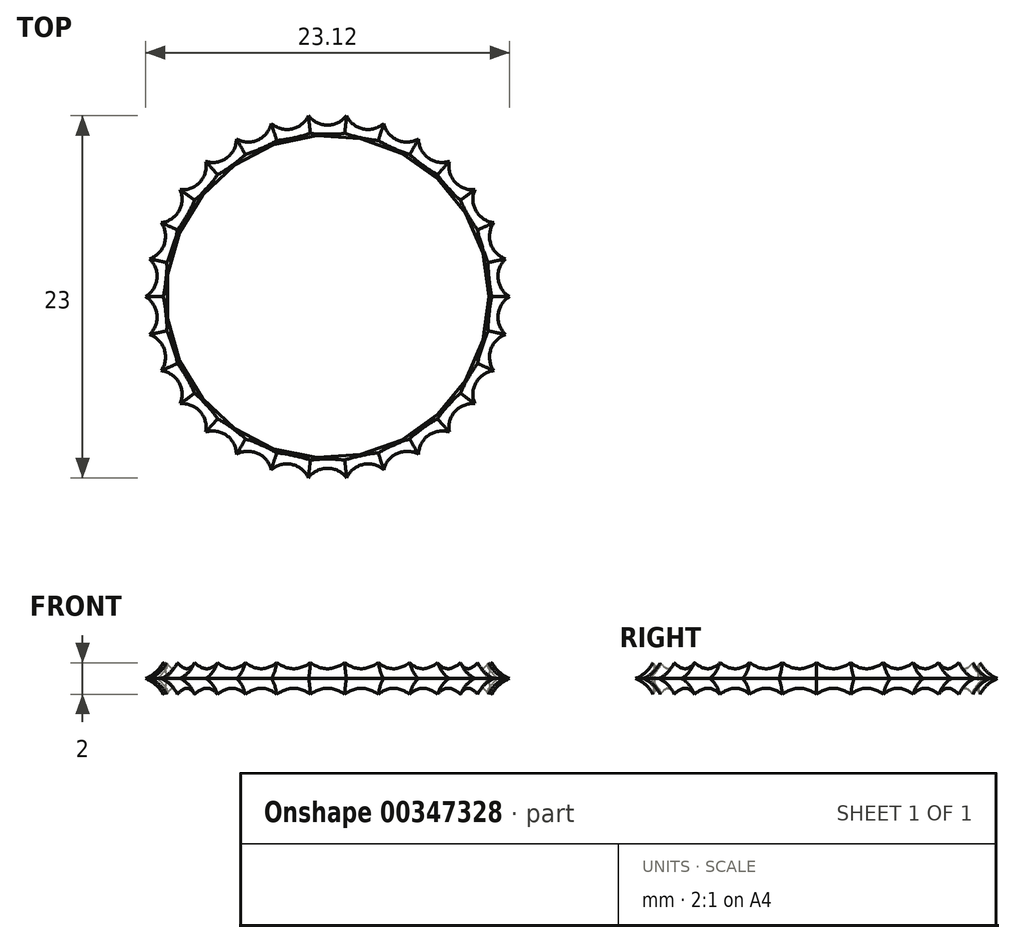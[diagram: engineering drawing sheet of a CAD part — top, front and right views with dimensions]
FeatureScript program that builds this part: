
annotation { "Feature Type Name" : "Feature", "Feature Type Description" : "" }
export const myFeature = defineFeature(function(context is Context, id is Id, definition is map)
    precondition{}
    {
        {
            var Q0;
            Q0=qCreatedBy(makeId("Front.planeOp"),FACE);
            var sketch = newSketch(context, id + "F0", { "sketchPlane" : qUnion([Q0])});
            skEllipse(sketch, "E0", {"center": v(11, 0) * mm, "majorRadius": 1.5 * mm, "minorRadius": 0.75 * mm, "majorAxis": v(0, 1)});
            skLineSegment(sketch, "E1", {"start": v(0, 20.87) * mm, "end": v(0, -23.5) * mm, "construction": true});
            skSolve(sketch);
        }
        {
            var Q0;
            Q0=makeQuery(id+"F0.imprint","IMPRINT",FACE,{"disambiguationData":[TD([[makeQuery(id+"F0.imprint","IMPRINT",EDGE,{"derivedFrom":sQuery(id+"F0.wireOp",EDGE,"E0")}),1.0]])]});
            var Q1;
            Q1=sQuery(id+"F0.wireOp",EDGE,"E1");
            revolve(context, id + "F1", {"entities" : qUnion([Q0]), "axis" : qUnion([Q1]), "revolveType" : RevolveType.FULL});
        }
        {
            var Q0;
            Q0=qCreatedBy(makeId("Right.planeOp"),FACE);
            var sketch = newSketch(context, id + "F2", { "sketchPlane" : qUnion([Q0])});
            skLineSegment(sketch, "E2", {"start": v(-11.23, 6.03) * mm, "end": v(-12.18, -4.75) * mm, "construction": true});
            skEllipse(sketch, "E3", {"center": v(-11, 0) * mm, "majorRadius": 1.5 * mm, "minorRadius": 0.75 * mm, "majorAxis": v(0, 1)});
            skLineSegment(sketch, "E4", {"start": v(-17.41, -3.3) * mm, "end": v(-16.66, 5.3) * mm});
            skSolve(sketch);
        }
        {
            var Q0;
            Q0=sQuery(id+"F2.wireOp",EDGE,"E4");
            cPlane(context, id + "F3", {"entities" : qUnion([Q0]), "cplaneType" : CPlaneType.LINE_ANGLE, "offset" : 25 * mm, "angle" : 90 * degree, "width" : 150 * mm, "height" : 150 * mm});
        }
        {
            var Q0;
            Q0=qCreatedBy(id+"F3.planeOp",FACE);
            var sketch = newSketch(context, id + "F4", { "sketchPlane" : qUnion([Q0])});
            skEllipticalArc(sketch, "E5", {});
            skPoint(sketch, "E6.firstSnap0", {"position": v(0, -8.8) * mm});
            skLineSegment(sketch, "E7", {"start": v(0, -3.31) * mm, "end": v(0, -10.23) * mm, "construction": true});
            skLineSegment(sketch, "E8", {"start": v(0, -3.8) * mm, "end": v(0, -8.8) * mm});
            const initialGuessF4  = {"E5": [0, -0.006309002116322518, 0, 1, 0.0025, 0.0025, 0, 3.141592653589793]};
            skSetInitialGuess(sketch, initialGuessF4);
            skSolve(sketch);
        }
        {
            var Q0;
            Q0 = qSketchRegion(id + "F4", true);
            var Q1;
            Q1=sQuery(id+"F2.wireOp",EDGE,"E4");
            revolve(context, id + "F5", {"entities" : qUnion([Q0]), "axis" : qUnion([Q1]), "revolveType" : RevolveType.FULL});
        }
        {
            var Q0;
            Q0=makeQuery(id+"F5.opRevolve","SWEPT_BODY",BODY,{"disambiguationData":[OSD([sQuery(id+"F4.wireOp",EDGE,"E5"),sQuery(id+"F4.wireOp",EDGE,"E8")])]});
            transform(context, id + "F6", {"entities" : qUnion([Q0]), "transformType" : TransformType.TRANSLATION_3D, "dx" : 0 * mm, "dy" : 5.14 * mm, "dz" : 6.8 * mm, "makeCopy" : false});
        }
        {
            var Q0;
            Q0=makeQuery(id+"F5.opRevolve","SWEPT_BODY",BODY,{"disambiguationData":[OSD([sQuery(id+"F4.wireOp",EDGE,"E5"),sQuery(id+"F4.wireOp",EDGE,"E8")])]});
            var Q1;
            Q1=sQuery(id+"F0.wireOp",EDGE,"E1");
            circularPattern(context, id + "F7", {"entities" : qUnion([Q0]), "axis" : qUnion([Q1]), "angle" : 360 * degree, "instanceCount" : 30, "equalSpace" : true});
        }
        {
            var Q0;
            Q0=makeQuery(id+"F5.opRevolve","SWEPT_BODY",BODY,{"disambiguationData":[OSD([sQuery(id+"F4.wireOp",EDGE,"E5"),sQuery(id+"F4.wireOp",EDGE,"E8")])]});
            var Q1;
            Q1=makeQuery(id+"F7.opPattern","COPY",BODY,{"derivedFrom":makeQuery(id+"F5.opRevolve","SWEPT_BODY",BODY,{"disambiguationData":[OSD([sQuery(id+"F4.wireOp",EDGE,"E5"),sQuery(id+"F4.wireOp",EDGE,"E8")])]}),"instanceName":"1"});
            var Q2;
            Q2=makeQuery(id+"F7.opPattern","COPY",BODY,{"derivedFrom":makeQuery(id+"F5.opRevolve","SWEPT_BODY",BODY,{"disambiguationData":[OSD([sQuery(id+"F4.wireOp",EDGE,"E5"),sQuery(id+"F4.wireOp",EDGE,"E8")])]}),"instanceName":"2"});
            var Q3;
            Q3=makeQuery(id+"F7.opPattern","COPY",BODY,{"derivedFrom":makeQuery(id+"F5.opRevolve","SWEPT_BODY",BODY,{"disambiguationData":[OSD([sQuery(id+"F4.wireOp",EDGE,"E5"),sQuery(id+"F4.wireOp",EDGE,"E8")])]}),"instanceName":"3"});
            var Q4;
            Q4=makeQuery(id+"F7.opPattern","COPY",BODY,{"derivedFrom":makeQuery(id+"F5.opRevolve","SWEPT_BODY",BODY,{"disambiguationData":[OSD([sQuery(id+"F4.wireOp",EDGE,"E5"),sQuery(id+"F4.wireOp",EDGE,"E8")])]}),"instanceName":"4"});
            var Q5;
            Q5=makeQuery(id+"F7.opPattern","COPY",BODY,{"derivedFrom":makeQuery(id+"F5.opRevolve","SWEPT_BODY",BODY,{"disambiguationData":[OSD([sQuery(id+"F4.wireOp",EDGE,"E5"),sQuery(id+"F4.wireOp",EDGE,"E8")])]}),"instanceName":"5"});
            var Q6;
            Q6=makeQuery(id+"F7.opPattern","COPY",BODY,{"derivedFrom":makeQuery(id+"F5.opRevolve","SWEPT_BODY",BODY,{"disambiguationData":[OSD([sQuery(id+"F4.wireOp",EDGE,"E5"),sQuery(id+"F4.wireOp",EDGE,"E8")])]}),"instanceName":"6"});
            var Q7;
            Q7=makeQuery(id+"F7.opPattern","COPY",BODY,{"derivedFrom":makeQuery(id+"F5.opRevolve","SWEPT_BODY",BODY,{"disambiguationData":[OSD([sQuery(id+"F4.wireOp",EDGE,"E5"),sQuery(id+"F4.wireOp",EDGE,"E8")])]}),"instanceName":"7"});
            var Q8;
            Q8=makeQuery(id+"F7.opPattern","COPY",BODY,{"derivedFrom":makeQuery(id+"F5.opRevolve","SWEPT_BODY",BODY,{"disambiguationData":[OSD([sQuery(id+"F4.wireOp",EDGE,"E5"),sQuery(id+"F4.wireOp",EDGE,"E8")])]}),"instanceName":"8"});
            var Q9;
            Q9=makeQuery(id+"F7.opPattern","COPY",BODY,{"derivedFrom":makeQuery(id+"F5.opRevolve","SWEPT_BODY",BODY,{"disambiguationData":[OSD([sQuery(id+"F4.wireOp",EDGE,"E5"),sQuery(id+"F4.wireOp",EDGE,"E8")])]}),"instanceName":"9"});
            var Q10;
            Q10=makeQuery(id+"F7.opPattern","COPY",BODY,{"derivedFrom":makeQuery(id+"F5.opRevolve","SWEPT_BODY",BODY,{"disambiguationData":[OSD([sQuery(id+"F4.wireOp",EDGE,"E5"),sQuery(id+"F4.wireOp",EDGE,"E8")])]}),"instanceName":"10"});
            var Q11;
            Q11=makeQuery(id+"F7.opPattern","COPY",BODY,{"derivedFrom":makeQuery(id+"F5.opRevolve","SWEPT_BODY",BODY,{"disambiguationData":[OSD([sQuery(id+"F4.wireOp",EDGE,"E5"),sQuery(id+"F4.wireOp",EDGE,"E8")])]}),"instanceName":"11"});
            var Q12;
            Q12=makeQuery(id+"F7.opPattern","COPY",BODY,{"derivedFrom":makeQuery(id+"F5.opRevolve","SWEPT_BODY",BODY,{"disambiguationData":[OSD([sQuery(id+"F4.wireOp",EDGE,"E5"),sQuery(id+"F4.wireOp",EDGE,"E8")])]}),"instanceName":"12"});
            var Q13;
            Q13=makeQuery(id+"F7.opPattern","COPY",BODY,{"derivedFrom":makeQuery(id+"F5.opRevolve","SWEPT_BODY",BODY,{"disambiguationData":[OSD([sQuery(id+"F4.wireOp",EDGE,"E5"),sQuery(id+"F4.wireOp",EDGE,"E8")])]}),"instanceName":"13"});
            var Q14;
            Q14=makeQuery(id+"F7.opPattern","COPY",BODY,{"derivedFrom":makeQuery(id+"F5.opRevolve","SWEPT_BODY",BODY,{"disambiguationData":[OSD([sQuery(id+"F4.wireOp",EDGE,"E5"),sQuery(id+"F4.wireOp",EDGE,"E8")])]}),"instanceName":"14"});
            var Q15;
            Q15=makeQuery(id+"F7.opPattern","COPY",BODY,{"derivedFrom":makeQuery(id+"F5.opRevolve","SWEPT_BODY",BODY,{"disambiguationData":[OSD([sQuery(id+"F4.wireOp",EDGE,"E5"),sQuery(id+"F4.wireOp",EDGE,"E8")])]}),"instanceName":"15"});
            var Q16;
            Q16=makeQuery(id+"F7.opPattern","COPY",BODY,{"derivedFrom":makeQuery(id+"F5.opRevolve","SWEPT_BODY",BODY,{"disambiguationData":[OSD([sQuery(id+"F4.wireOp",EDGE,"E5"),sQuery(id+"F4.wireOp",EDGE,"E8")])]}),"instanceName":"16"});
            var Q17;
            Q17=makeQuery(id+"F7.opPattern","COPY",BODY,{"derivedFrom":makeQuery(id+"F5.opRevolve","SWEPT_BODY",BODY,{"disambiguationData":[OSD([sQuery(id+"F4.wireOp",EDGE,"E5"),sQuery(id+"F4.wireOp",EDGE,"E8")])]}),"instanceName":"17"});
            var Q18;
            Q18=makeQuery(id+"F7.opPattern","COPY",BODY,{"derivedFrom":makeQuery(id+"F5.opRevolve","SWEPT_BODY",BODY,{"disambiguationData":[OSD([sQuery(id+"F4.wireOp",EDGE,"E5"),sQuery(id+"F4.wireOp",EDGE,"E8")])]}),"instanceName":"18"});
            var Q19;
            Q19=makeQuery(id+"F7.opPattern","COPY",BODY,{"derivedFrom":makeQuery(id+"F5.opRevolve","SWEPT_BODY",BODY,{"disambiguationData":[OSD([sQuery(id+"F4.wireOp",EDGE,"E5"),sQuery(id+"F4.wireOp",EDGE,"E8")])]}),"instanceName":"19"});
            var Q20;
            Q20=makeQuery(id+"F7.opPattern","COPY",BODY,{"derivedFrom":makeQuery(id+"F5.opRevolve","SWEPT_BODY",BODY,{"disambiguationData":[OSD([sQuery(id+"F4.wireOp",EDGE,"E5"),sQuery(id+"F4.wireOp",EDGE,"E8")])]}),"instanceName":"20"});
            var Q21;
            Q21=makeQuery(id+"F7.opPattern","COPY",BODY,{"derivedFrom":makeQuery(id+"F5.opRevolve","SWEPT_BODY",BODY,{"disambiguationData":[OSD([sQuery(id+"F4.wireOp",EDGE,"E5"),sQuery(id+"F4.wireOp",EDGE,"E8")])]}),"instanceName":"21"});
            var Q22;
            Q22=makeQuery(id+"F7.opPattern","COPY",BODY,{"derivedFrom":makeQuery(id+"F5.opRevolve","SWEPT_BODY",BODY,{"disambiguationData":[OSD([sQuery(id+"F4.wireOp",EDGE,"E5"),sQuery(id+"F4.wireOp",EDGE,"E8")])]}),"instanceName":"22"});
            var Q23;
            Q23=makeQuery(id+"F7.opPattern","COPY",BODY,{"derivedFrom":makeQuery(id+"F5.opRevolve","SWEPT_BODY",BODY,{"disambiguationData":[OSD([sQuery(id+"F4.wireOp",EDGE,"E5"),sQuery(id+"F4.wireOp",EDGE,"E8")])]}),"instanceName":"23"});
            var Q24;
            Q24=makeQuery(id+"F7.opPattern","COPY",BODY,{"derivedFrom":makeQuery(id+"F5.opRevolve","SWEPT_BODY",BODY,{"disambiguationData":[OSD([sQuery(id+"F4.wireOp",EDGE,"E5"),sQuery(id+"F4.wireOp",EDGE,"E8")])]}),"instanceName":"24"});
            var Q25;
            Q25=makeQuery(id+"F7.opPattern","COPY",BODY,{"derivedFrom":makeQuery(id+"F5.opRevolve","SWEPT_BODY",BODY,{"disambiguationData":[OSD([sQuery(id+"F4.wireOp",EDGE,"E5"),sQuery(id+"F4.wireOp",EDGE,"E8")])]}),"instanceName":"25"});
            var Q26;
            Q26=makeQuery(id+"F7.opPattern","COPY",BODY,{"derivedFrom":makeQuery(id+"F5.opRevolve","SWEPT_BODY",BODY,{"disambiguationData":[OSD([sQuery(id+"F4.wireOp",EDGE,"E5"),sQuery(id+"F4.wireOp",EDGE,"E8")])]}),"instanceName":"26"});
            var Q27;
            Q27=makeQuery(id+"F7.opPattern","COPY",BODY,{"derivedFrom":makeQuery(id+"F5.opRevolve","SWEPT_BODY",BODY,{"disambiguationData":[OSD([sQuery(id+"F4.wireOp",EDGE,"E5"),sQuery(id+"F4.wireOp",EDGE,"E8")])]}),"instanceName":"27"});
            var Q28;
            Q28=makeQuery(id+"F7.opPattern","COPY",BODY,{"derivedFrom":makeQuery(id+"F5.opRevolve","SWEPT_BODY",BODY,{"disambiguationData":[OSD([sQuery(id+"F4.wireOp",EDGE,"E5"),sQuery(id+"F4.wireOp",EDGE,"E8")])]}),"instanceName":"28"});
            var Q29;
            Q29=makeQuery(id+"F7.opPattern","COPY",BODY,{"derivedFrom":makeQuery(id+"F5.opRevolve","SWEPT_BODY",BODY,{"disambiguationData":[OSD([sQuery(id+"F4.wireOp",EDGE,"E5"),sQuery(id+"F4.wireOp",EDGE,"E8")])]}),"instanceName":"29"});
            var Q30;
            Q30=qCreatedBy(makeId("Top.planeOp"),FACE);
            mirror(context, id + "F8", {"entities" : qUnion([Q0, Q1, Q2, Q3, Q4, Q5, Q6, Q7, Q8, Q9, Q10, Q11, Q12, Q13, Q14, Q15, Q16, Q17, Q18, Q19, Q20, Q21, Q22, Q23, Q24, Q25, Q26, Q27, Q28, Q29]), "mirrorPlane" : qUnion([Q30])});
        }
        {
            var Q0;
            Q0=makeQuery(id+"F5.opRevolve","SWEPT_BODY",BODY,{"disambiguationData":[OSD([sQuery(id+"F4.wireOp",EDGE,"E5"),sQuery(id+"F4.wireOp",EDGE,"E8")])]});
            var Q1;
            Q1=makeQuery(id+"F7.opPattern","COPY",BODY,{"derivedFrom":makeQuery(id+"F5.opRevolve","SWEPT_BODY",BODY,{"disambiguationData":[OSD([sQuery(id+"F4.wireOp",EDGE,"E5"),sQuery(id+"F4.wireOp",EDGE,"E8")])]}),"instanceName":"1"});
            var Q2;
            Q2=makeQuery(id+"F7.opPattern","COPY",BODY,{"derivedFrom":makeQuery(id+"F5.opRevolve","SWEPT_BODY",BODY,{"disambiguationData":[OSD([sQuery(id+"F4.wireOp",EDGE,"E5"),sQuery(id+"F4.wireOp",EDGE,"E8")])]}),"instanceName":"2"});
            var Q3;
            Q3=makeQuery(id+"F7.opPattern","COPY",BODY,{"derivedFrom":makeQuery(id+"F5.opRevolve","SWEPT_BODY",BODY,{"disambiguationData":[OSD([sQuery(id+"F4.wireOp",EDGE,"E5"),sQuery(id+"F4.wireOp",EDGE,"E8")])]}),"instanceName":"3"});
            var Q4;
            Q4=makeQuery(id+"F7.opPattern","COPY",BODY,{"derivedFrom":makeQuery(id+"F5.opRevolve","SWEPT_BODY",BODY,{"disambiguationData":[OSD([sQuery(id+"F4.wireOp",EDGE,"E5"),sQuery(id+"F4.wireOp",EDGE,"E8")])]}),"instanceName":"4"});
            var Q5;
            Q5=makeQuery(id+"F7.opPattern","COPY",BODY,{"derivedFrom":makeQuery(id+"F5.opRevolve","SWEPT_BODY",BODY,{"disambiguationData":[OSD([sQuery(id+"F4.wireOp",EDGE,"E5"),sQuery(id+"F4.wireOp",EDGE,"E8")])]}),"instanceName":"5"});
            var Q6;
            Q6=makeQuery(id+"F7.opPattern","COPY",BODY,{"derivedFrom":makeQuery(id+"F5.opRevolve","SWEPT_BODY",BODY,{"disambiguationData":[OSD([sQuery(id+"F4.wireOp",EDGE,"E5"),sQuery(id+"F4.wireOp",EDGE,"E8")])]}),"instanceName":"6"});
            var Q7;
            Q7=makeQuery(id+"F7.opPattern","COPY",BODY,{"derivedFrom":makeQuery(id+"F5.opRevolve","SWEPT_BODY",BODY,{"disambiguationData":[OSD([sQuery(id+"F4.wireOp",EDGE,"E5"),sQuery(id+"F4.wireOp",EDGE,"E8")])]}),"instanceName":"7"});
            var Q8;
            Q8=makeQuery(id+"F7.opPattern","COPY",BODY,{"derivedFrom":makeQuery(id+"F5.opRevolve","SWEPT_BODY",BODY,{"disambiguationData":[OSD([sQuery(id+"F4.wireOp",EDGE,"E5"),sQuery(id+"F4.wireOp",EDGE,"E8")])]}),"instanceName":"8"});
            var Q9;
            Q9=makeQuery(id+"F7.opPattern","COPY",BODY,{"derivedFrom":makeQuery(id+"F5.opRevolve","SWEPT_BODY",BODY,{"disambiguationData":[OSD([sQuery(id+"F4.wireOp",EDGE,"E5"),sQuery(id+"F4.wireOp",EDGE,"E8")])]}),"instanceName":"9"});
            var Q10;
            Q10=makeQuery(id+"F7.opPattern","COPY",BODY,{"derivedFrom":makeQuery(id+"F5.opRevolve","SWEPT_BODY",BODY,{"disambiguationData":[OSD([sQuery(id+"F4.wireOp",EDGE,"E5"),sQuery(id+"F4.wireOp",EDGE,"E8")])]}),"instanceName":"10"});
            var Q11;
            Q11=makeQuery(id+"F7.opPattern","COPY",BODY,{"derivedFrom":makeQuery(id+"F5.opRevolve","SWEPT_BODY",BODY,{"disambiguationData":[OSD([sQuery(id+"F4.wireOp",EDGE,"E5"),sQuery(id+"F4.wireOp",EDGE,"E8")])]}),"instanceName":"11"});
            var Q12;
            Q12=makeQuery(id+"F7.opPattern","COPY",BODY,{"derivedFrom":makeQuery(id+"F5.opRevolve","SWEPT_BODY",BODY,{"disambiguationData":[OSD([sQuery(id+"F4.wireOp",EDGE,"E5"),sQuery(id+"F4.wireOp",EDGE,"E8")])]}),"instanceName":"12"});
            var Q13;
            Q13=makeQuery(id+"F7.opPattern","COPY",BODY,{"derivedFrom":makeQuery(id+"F5.opRevolve","SWEPT_BODY",BODY,{"disambiguationData":[OSD([sQuery(id+"F4.wireOp",EDGE,"E5"),sQuery(id+"F4.wireOp",EDGE,"E8")])]}),"instanceName":"13"});
            var Q14;
            Q14=makeQuery(id+"F7.opPattern","COPY",BODY,{"derivedFrom":makeQuery(id+"F5.opRevolve","SWEPT_BODY",BODY,{"disambiguationData":[OSD([sQuery(id+"F4.wireOp",EDGE,"E5"),sQuery(id+"F4.wireOp",EDGE,"E8")])]}),"instanceName":"14"});
            var Q15;
            Q15=makeQuery(id+"F7.opPattern","COPY",BODY,{"derivedFrom":makeQuery(id+"F5.opRevolve","SWEPT_BODY",BODY,{"disambiguationData":[OSD([sQuery(id+"F4.wireOp",EDGE,"E5"),sQuery(id+"F4.wireOp",EDGE,"E8")])]}),"instanceName":"15"});
            var Q16;
            Q16=makeQuery(id+"F7.opPattern","COPY",BODY,{"derivedFrom":makeQuery(id+"F5.opRevolve","SWEPT_BODY",BODY,{"disambiguationData":[OSD([sQuery(id+"F4.wireOp",EDGE,"E5"),sQuery(id+"F4.wireOp",EDGE,"E8")])]}),"instanceName":"16"});
            var Q17;
            Q17=makeQuery(id+"F7.opPattern","COPY",BODY,{"derivedFrom":makeQuery(id+"F5.opRevolve","SWEPT_BODY",BODY,{"disambiguationData":[OSD([sQuery(id+"F4.wireOp",EDGE,"E5"),sQuery(id+"F4.wireOp",EDGE,"E8")])]}),"instanceName":"17"});
            var Q18;
            Q18=makeQuery(id+"F7.opPattern","COPY",BODY,{"derivedFrom":makeQuery(id+"F5.opRevolve","SWEPT_BODY",BODY,{"disambiguationData":[OSD([sQuery(id+"F4.wireOp",EDGE,"E5"),sQuery(id+"F4.wireOp",EDGE,"E8")])]}),"instanceName":"18"});
            var Q19;
            Q19=makeQuery(id+"F7.opPattern","COPY",BODY,{"derivedFrom":makeQuery(id+"F5.opRevolve","SWEPT_BODY",BODY,{"disambiguationData":[OSD([sQuery(id+"F4.wireOp",EDGE,"E5"),sQuery(id+"F4.wireOp",EDGE,"E8")])]}),"instanceName":"19"});
            var Q20;
            Q20=makeQuery(id+"F7.opPattern","COPY",BODY,{"derivedFrom":makeQuery(id+"F5.opRevolve","SWEPT_BODY",BODY,{"disambiguationData":[OSD([sQuery(id+"F4.wireOp",EDGE,"E5"),sQuery(id+"F4.wireOp",EDGE,"E8")])]}),"instanceName":"20"});
            var Q21;
            Q21=makeQuery(id+"F7.opPattern","COPY",BODY,{"derivedFrom":makeQuery(id+"F5.opRevolve","SWEPT_BODY",BODY,{"disambiguationData":[OSD([sQuery(id+"F4.wireOp",EDGE,"E5"),sQuery(id+"F4.wireOp",EDGE,"E8")])]}),"instanceName":"21"});
            var Q22;
            Q22=makeQuery(id+"F7.opPattern","COPY",BODY,{"derivedFrom":makeQuery(id+"F5.opRevolve","SWEPT_BODY",BODY,{"disambiguationData":[OSD([sQuery(id+"F4.wireOp",EDGE,"E5"),sQuery(id+"F4.wireOp",EDGE,"E8")])]}),"instanceName":"22"});
            var Q23;
            Q23=makeQuery(id+"F7.opPattern","COPY",BODY,{"derivedFrom":makeQuery(id+"F5.opRevolve","SWEPT_BODY",BODY,{"disambiguationData":[OSD([sQuery(id+"F4.wireOp",EDGE,"E5"),sQuery(id+"F4.wireOp",EDGE,"E8")])]}),"instanceName":"23"});
            var Q24;
            Q24=makeQuery(id+"F7.opPattern","COPY",BODY,{"derivedFrom":makeQuery(id+"F5.opRevolve","SWEPT_BODY",BODY,{"disambiguationData":[OSD([sQuery(id+"F4.wireOp",EDGE,"E5"),sQuery(id+"F4.wireOp",EDGE,"E8")])]}),"instanceName":"24"});
            var Q25;
            Q25=makeQuery(id+"F7.opPattern","COPY",BODY,{"derivedFrom":makeQuery(id+"F5.opRevolve","SWEPT_BODY",BODY,{"disambiguationData":[OSD([sQuery(id+"F4.wireOp",EDGE,"E5"),sQuery(id+"F4.wireOp",EDGE,"E8")])]}),"instanceName":"25"});
            var Q26;
            Q26=makeQuery(id+"F7.opPattern","COPY",BODY,{"derivedFrom":makeQuery(id+"F5.opRevolve","SWEPT_BODY",BODY,{"disambiguationData":[OSD([sQuery(id+"F4.wireOp",EDGE,"E5"),sQuery(id+"F4.wireOp",EDGE,"E8")])]}),"instanceName":"26"});
            var Q27;
            Q27=makeQuery(id+"F7.opPattern","COPY",BODY,{"derivedFrom":makeQuery(id+"F5.opRevolve","SWEPT_BODY",BODY,{"disambiguationData":[OSD([sQuery(id+"F4.wireOp",EDGE,"E5"),sQuery(id+"F4.wireOp",EDGE,"E8")])]}),"instanceName":"27"});
            var Q28;
            Q28=makeQuery(id+"F7.opPattern","COPY",BODY,{"derivedFrom":makeQuery(id+"F5.opRevolve","SWEPT_BODY",BODY,{"disambiguationData":[OSD([sQuery(id+"F4.wireOp",EDGE,"E5"),sQuery(id+"F4.wireOp",EDGE,"E8")])]}),"instanceName":"28"});
            var Q29;
            Q29=makeQuery(id+"F7.opPattern","COPY",BODY,{"derivedFrom":makeQuery(id+"F5.opRevolve","SWEPT_BODY",BODY,{"disambiguationData":[OSD([sQuery(id+"F4.wireOp",EDGE,"E5"),sQuery(id+"F4.wireOp",EDGE,"E8")])]}),"instanceName":"29"});
            var Q30;
            Q30=makeQuery(id+"F8.opPattern","COPY",BODY,{"derivedFrom":makeQuery(id+"F5.opRevolve","SWEPT_BODY",BODY,{"disambiguationData":[OSD([sQuery(id+"F4.wireOp",EDGE,"E5"),sQuery(id+"F4.wireOp",EDGE,"E8")])]}),"instanceName":"1"});
            var Q31;
            Q31=makeQuery(id+"F8.opPattern","COPY",BODY,{"derivedFrom":makeQuery(id+"F7.opPattern","COPY",BODY,{"derivedFrom":makeQuery(id+"F5.opRevolve","SWEPT_BODY",BODY,{"disambiguationData":[OSD([sQuery(id+"F4.wireOp",EDGE,"E5"),sQuery(id+"F4.wireOp",EDGE,"E8")])]}),"instanceName":"1"}),"instanceName":"1"});
            var Q32;
            Q32=makeQuery(id+"F8.opPattern","COPY",BODY,{"derivedFrom":makeQuery(id+"F7.opPattern","COPY",BODY,{"derivedFrom":makeQuery(id+"F5.opRevolve","SWEPT_BODY",BODY,{"disambiguationData":[OSD([sQuery(id+"F4.wireOp",EDGE,"E5"),sQuery(id+"F4.wireOp",EDGE,"E8")])]}),"instanceName":"2"}),"instanceName":"1"});
            var Q33;
            Q33=makeQuery(id+"F8.opPattern","COPY",BODY,{"derivedFrom":makeQuery(id+"F7.opPattern","COPY",BODY,{"derivedFrom":makeQuery(id+"F5.opRevolve","SWEPT_BODY",BODY,{"disambiguationData":[OSD([sQuery(id+"F4.wireOp",EDGE,"E5"),sQuery(id+"F4.wireOp",EDGE,"E8")])]}),"instanceName":"3"}),"instanceName":"1"});
            var Q34;
            Q34=makeQuery(id+"F8.opPattern","COPY",BODY,{"derivedFrom":makeQuery(id+"F7.opPattern","COPY",BODY,{"derivedFrom":makeQuery(id+"F5.opRevolve","SWEPT_BODY",BODY,{"disambiguationData":[OSD([sQuery(id+"F4.wireOp",EDGE,"E5"),sQuery(id+"F4.wireOp",EDGE,"E8")])]}),"instanceName":"4"}),"instanceName":"1"});
            var Q35;
            Q35=makeQuery(id+"F8.opPattern","COPY",BODY,{"derivedFrom":makeQuery(id+"F7.opPattern","COPY",BODY,{"derivedFrom":makeQuery(id+"F5.opRevolve","SWEPT_BODY",BODY,{"disambiguationData":[OSD([sQuery(id+"F4.wireOp",EDGE,"E5"),sQuery(id+"F4.wireOp",EDGE,"E8")])]}),"instanceName":"5"}),"instanceName":"1"});
            var Q36;
            Q36=makeQuery(id+"F8.opPattern","COPY",BODY,{"derivedFrom":makeQuery(id+"F7.opPattern","COPY",BODY,{"derivedFrom":makeQuery(id+"F5.opRevolve","SWEPT_BODY",BODY,{"disambiguationData":[OSD([sQuery(id+"F4.wireOp",EDGE,"E5"),sQuery(id+"F4.wireOp",EDGE,"E8")])]}),"instanceName":"6"}),"instanceName":"1"});
            var Q37;
            Q37=makeQuery(id+"F8.opPattern","COPY",BODY,{"derivedFrom":makeQuery(id+"F7.opPattern","COPY",BODY,{"derivedFrom":makeQuery(id+"F5.opRevolve","SWEPT_BODY",BODY,{"disambiguationData":[OSD([sQuery(id+"F4.wireOp",EDGE,"E5"),sQuery(id+"F4.wireOp",EDGE,"E8")])]}),"instanceName":"7"}),"instanceName":"1"});
            var Q38;
            Q38=makeQuery(id+"F8.opPattern","COPY",BODY,{"derivedFrom":makeQuery(id+"F7.opPattern","COPY",BODY,{"derivedFrom":makeQuery(id+"F5.opRevolve","SWEPT_BODY",BODY,{"disambiguationData":[OSD([sQuery(id+"F4.wireOp",EDGE,"E5"),sQuery(id+"F4.wireOp",EDGE,"E8")])]}),"instanceName":"8"}),"instanceName":"1"});
            var Q39;
            Q39=makeQuery(id+"F8.opPattern","COPY",BODY,{"derivedFrom":makeQuery(id+"F7.opPattern","COPY",BODY,{"derivedFrom":makeQuery(id+"F5.opRevolve","SWEPT_BODY",BODY,{"disambiguationData":[OSD([sQuery(id+"F4.wireOp",EDGE,"E5"),sQuery(id+"F4.wireOp",EDGE,"E8")])]}),"instanceName":"9"}),"instanceName":"1"});
            var Q40;
            Q40=makeQuery(id+"F8.opPattern","COPY",BODY,{"derivedFrom":makeQuery(id+"F7.opPattern","COPY",BODY,{"derivedFrom":makeQuery(id+"F5.opRevolve","SWEPT_BODY",BODY,{"disambiguationData":[OSD([sQuery(id+"F4.wireOp",EDGE,"E5"),sQuery(id+"F4.wireOp",EDGE,"E8")])]}),"instanceName":"10"}),"instanceName":"1"});
            var Q41;
            Q41=makeQuery(id+"F8.opPattern","COPY",BODY,{"derivedFrom":makeQuery(id+"F7.opPattern","COPY",BODY,{"derivedFrom":makeQuery(id+"F5.opRevolve","SWEPT_BODY",BODY,{"disambiguationData":[OSD([sQuery(id+"F4.wireOp",EDGE,"E5"),sQuery(id+"F4.wireOp",EDGE,"E8")])]}),"instanceName":"11"}),"instanceName":"1"});
            var Q42;
            Q42=makeQuery(id+"F8.opPattern","COPY",BODY,{"derivedFrom":makeQuery(id+"F7.opPattern","COPY",BODY,{"derivedFrom":makeQuery(id+"F5.opRevolve","SWEPT_BODY",BODY,{"disambiguationData":[OSD([sQuery(id+"F4.wireOp",EDGE,"E5"),sQuery(id+"F4.wireOp",EDGE,"E8")])]}),"instanceName":"12"}),"instanceName":"1"});
            var Q43;
            Q43=makeQuery(id+"F8.opPattern","COPY",BODY,{"derivedFrom":makeQuery(id+"F7.opPattern","COPY",BODY,{"derivedFrom":makeQuery(id+"F5.opRevolve","SWEPT_BODY",BODY,{"disambiguationData":[OSD([sQuery(id+"F4.wireOp",EDGE,"E5"),sQuery(id+"F4.wireOp",EDGE,"E8")])]}),"instanceName":"13"}),"instanceName":"1"});
            var Q44;
            Q44=makeQuery(id+"F8.opPattern","COPY",BODY,{"derivedFrom":makeQuery(id+"F7.opPattern","COPY",BODY,{"derivedFrom":makeQuery(id+"F5.opRevolve","SWEPT_BODY",BODY,{"disambiguationData":[OSD([sQuery(id+"F4.wireOp",EDGE,"E5"),sQuery(id+"F4.wireOp",EDGE,"E8")])]}),"instanceName":"14"}),"instanceName":"1"});
            var Q45;
            Q45=makeQuery(id+"F8.opPattern","COPY",BODY,{"derivedFrom":makeQuery(id+"F7.opPattern","COPY",BODY,{"derivedFrom":makeQuery(id+"F5.opRevolve","SWEPT_BODY",BODY,{"disambiguationData":[OSD([sQuery(id+"F4.wireOp",EDGE,"E5"),sQuery(id+"F4.wireOp",EDGE,"E8")])]}),"instanceName":"15"}),"instanceName":"1"});
            var Q46;
            Q46=makeQuery(id+"F8.opPattern","COPY",BODY,{"derivedFrom":makeQuery(id+"F7.opPattern","COPY",BODY,{"derivedFrom":makeQuery(id+"F5.opRevolve","SWEPT_BODY",BODY,{"disambiguationData":[OSD([sQuery(id+"F4.wireOp",EDGE,"E5"),sQuery(id+"F4.wireOp",EDGE,"E8")])]}),"instanceName":"16"}),"instanceName":"1"});
            var Q47;
            Q47=makeQuery(id+"F8.opPattern","COPY",BODY,{"derivedFrom":makeQuery(id+"F7.opPattern","COPY",BODY,{"derivedFrom":makeQuery(id+"F5.opRevolve","SWEPT_BODY",BODY,{"disambiguationData":[OSD([sQuery(id+"F4.wireOp",EDGE,"E5"),sQuery(id+"F4.wireOp",EDGE,"E8")])]}),"instanceName":"17"}),"instanceName":"1"});
            var Q48;
            Q48=makeQuery(id+"F8.opPattern","COPY",BODY,{"derivedFrom":makeQuery(id+"F7.opPattern","COPY",BODY,{"derivedFrom":makeQuery(id+"F5.opRevolve","SWEPT_BODY",BODY,{"disambiguationData":[OSD([sQuery(id+"F4.wireOp",EDGE,"E5"),sQuery(id+"F4.wireOp",EDGE,"E8")])]}),"instanceName":"18"}),"instanceName":"1"});
            var Q49;
            Q49=makeQuery(id+"F8.opPattern","COPY",BODY,{"derivedFrom":makeQuery(id+"F7.opPattern","COPY",BODY,{"derivedFrom":makeQuery(id+"F5.opRevolve","SWEPT_BODY",BODY,{"disambiguationData":[OSD([sQuery(id+"F4.wireOp",EDGE,"E5"),sQuery(id+"F4.wireOp",EDGE,"E8")])]}),"instanceName":"19"}),"instanceName":"1"});
            var Q50;
            Q50=makeQuery(id+"F8.opPattern","COPY",BODY,{"derivedFrom":makeQuery(id+"F7.opPattern","COPY",BODY,{"derivedFrom":makeQuery(id+"F5.opRevolve","SWEPT_BODY",BODY,{"disambiguationData":[OSD([sQuery(id+"F4.wireOp",EDGE,"E5"),sQuery(id+"F4.wireOp",EDGE,"E8")])]}),"instanceName":"20"}),"instanceName":"1"});
            var Q51;
            Q51=makeQuery(id+"F8.opPattern","COPY",BODY,{"derivedFrom":makeQuery(id+"F7.opPattern","COPY",BODY,{"derivedFrom":makeQuery(id+"F5.opRevolve","SWEPT_BODY",BODY,{"disambiguationData":[OSD([sQuery(id+"F4.wireOp",EDGE,"E5"),sQuery(id+"F4.wireOp",EDGE,"E8")])]}),"instanceName":"21"}),"instanceName":"1"});
            var Q52;
            Q52=makeQuery(id+"F8.opPattern","COPY",BODY,{"derivedFrom":makeQuery(id+"F7.opPattern","COPY",BODY,{"derivedFrom":makeQuery(id+"F5.opRevolve","SWEPT_BODY",BODY,{"disambiguationData":[OSD([sQuery(id+"F4.wireOp",EDGE,"E5"),sQuery(id+"F4.wireOp",EDGE,"E8")])]}),"instanceName":"22"}),"instanceName":"1"});
            var Q53;
            Q53=makeQuery(id+"F8.opPattern","COPY",BODY,{"derivedFrom":makeQuery(id+"F7.opPattern","COPY",BODY,{"derivedFrom":makeQuery(id+"F5.opRevolve","SWEPT_BODY",BODY,{"disambiguationData":[OSD([sQuery(id+"F4.wireOp",EDGE,"E5"),sQuery(id+"F4.wireOp",EDGE,"E8")])]}),"instanceName":"23"}),"instanceName":"1"});
            var Q54;
            Q54=makeQuery(id+"F8.opPattern","COPY",BODY,{"derivedFrom":makeQuery(id+"F7.opPattern","COPY",BODY,{"derivedFrom":makeQuery(id+"F5.opRevolve","SWEPT_BODY",BODY,{"disambiguationData":[OSD([sQuery(id+"F4.wireOp",EDGE,"E5"),sQuery(id+"F4.wireOp",EDGE,"E8")])]}),"instanceName":"24"}),"instanceName":"1"});
            var Q55;
            Q55=makeQuery(id+"F8.opPattern","COPY",BODY,{"derivedFrom":makeQuery(id+"F7.opPattern","COPY",BODY,{"derivedFrom":makeQuery(id+"F5.opRevolve","SWEPT_BODY",BODY,{"disambiguationData":[OSD([sQuery(id+"F4.wireOp",EDGE,"E5"),sQuery(id+"F4.wireOp",EDGE,"E8")])]}),"instanceName":"25"}),"instanceName":"1"});
            var Q56;
            Q56=makeQuery(id+"F8.opPattern","COPY",BODY,{"derivedFrom":makeQuery(id+"F7.opPattern","COPY",BODY,{"derivedFrom":makeQuery(id+"F5.opRevolve","SWEPT_BODY",BODY,{"disambiguationData":[OSD([sQuery(id+"F4.wireOp",EDGE,"E5"),sQuery(id+"F4.wireOp",EDGE,"E8")])]}),"instanceName":"26"}),"instanceName":"1"});
            var Q57;
            Q57=makeQuery(id+"F8.opPattern","COPY",BODY,{"derivedFrom":makeQuery(id+"F7.opPattern","COPY",BODY,{"derivedFrom":makeQuery(id+"F5.opRevolve","SWEPT_BODY",BODY,{"disambiguationData":[OSD([sQuery(id+"F4.wireOp",EDGE,"E5"),sQuery(id+"F4.wireOp",EDGE,"E8")])]}),"instanceName":"27"}),"instanceName":"1"});
            var Q58;
            Q58=makeQuery(id+"F8.opPattern","COPY",BODY,{"derivedFrom":makeQuery(id+"F7.opPattern","COPY",BODY,{"derivedFrom":makeQuery(id+"F5.opRevolve","SWEPT_BODY",BODY,{"disambiguationData":[OSD([sQuery(id+"F4.wireOp",EDGE,"E5"),sQuery(id+"F4.wireOp",EDGE,"E8")])]}),"instanceName":"28"}),"instanceName":"1"});
            var Q59;
            Q59=makeQuery(id+"F8.opPattern","COPY",BODY,{"derivedFrom":makeQuery(id+"F7.opPattern","COPY",BODY,{"derivedFrom":makeQuery(id+"F5.opRevolve","SWEPT_BODY",BODY,{"disambiguationData":[OSD([sQuery(id+"F4.wireOp",EDGE,"E5"),sQuery(id+"F4.wireOp",EDGE,"E8")])]}),"instanceName":"29"}),"instanceName":"1"});
            var Q60;
            Q60=makeQuery(id+"F1.opRevolve","SWEPT_BODY",BODY,{"disambiguationData":[OSD([sQuery(id+"F0.wireOp",EDGE,"E0")])]});
            booleanBodies(context, id + "F9", {"operationType" : BooleanOperationType.SUBTRACTION, "tools" : qUnion([Q0, Q1, Q2, Q3, Q4, Q5, Q6, Q7, Q8, Q9, Q10, Q11, Q12, Q13, Q14, Q15, Q16, Q17, Q18, Q19, Q20, Q21, Q22, Q23, Q24, Q25, Q26, Q27, Q28, Q29, Q30, Q31, Q32, Q33, Q34, Q35, Q36, Q37, Q38, Q39, Q40, Q41, Q42, Q43, Q44, Q45, Q46, Q47, Q48, Q49, Q50, Q51, Q52, Q53, Q54, Q55, Q56, Q57, Q58, Q59]), "targets" : qUnion([Q60])});
        }
    });
